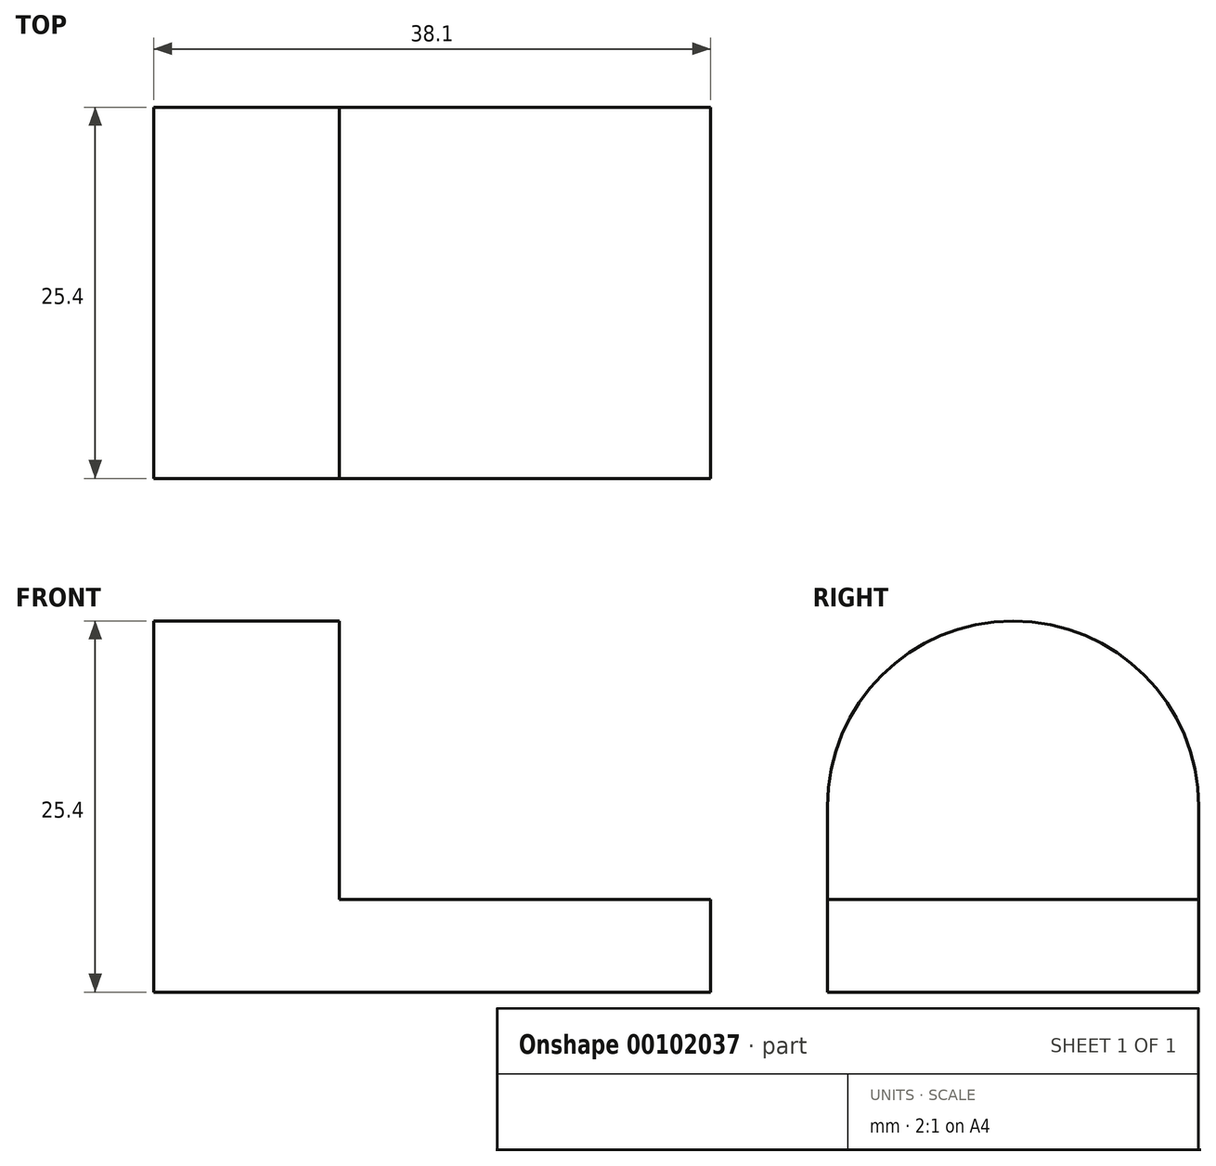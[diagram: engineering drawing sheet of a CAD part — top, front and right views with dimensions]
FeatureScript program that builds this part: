
annotation { "Feature Type Name" : "Feature", "Feature Type Description" : "" }
export const myFeature = defineFeature(function(context is Context, id is Id, definition is map)
    precondition{}
    {
        {
            var Q0;
            Q0=qCreatedBy(makeId("Right.planeOp"),FACE);
            var sketch = newSketch(context, id + "F0", { "sketchPlane" : qUnion([Q0])});
            skLineSegment(sketch, "E0", {"start": v(0, 0) * mm, "end": v(0, 12.7) * mm});
            skLineSegment(sketch, "E1", {"start": v(0, 0) * mm, "end": v(25.4, 0) * mm});
            skLineSegment(sketch, "E2", {"start": v(25.4, 0) * mm, "end": v(25.4, 12.7) * mm});
            skArc(sketch, "E3", {"start": v(25.4, 12.7) * mm, "mid": v(12.7, 25.4) * mm, "end": v(0, 12.7) * mm});
            skSolve(sketch);
        }
        {
            var Q0;
            Q0 = qSketchRegion(id + "F0", true);
            extrude(context, id + "F1", {"entities" : qUnion([Q0]), "depth" : 12.7 * mm});
        }
        {
            var Q0;
            Q0=makeQuery(id+"F1.opExtrude","CAP_FACE",FACE,{"disambiguationData":[OSD([sQuery(id+"F0.wireOp",EDGE,"E0"),sQuery(id+"F0.wireOp",EDGE,"E1"),sQuery(id+"F0.wireOp",EDGE,"E2"),sQuery(id+"F0.wireOp",EDGE,"E3")])],"isStart":false});
            var sketch = newSketch(context, id + "F2", { "sketchPlane" : qUnion([Q0])});
            skLineSegment(sketch, "E4.bottom", {"start": v(0, 0) * mm, "end": v(25.4, 0) * mm});
            skLineSegment(sketch, "E4.top", {"start": v(0, 6.35) * mm, "end": v(25.4, 6.35) * mm});
            skLineSegment(sketch, "E4.left", {"start": v(0, 0) * mm, "end": v(0, 6.35) * mm});
            skLineSegment(sketch, "E4.right", {"start": v(25.4, 0) * mm, "end": v(25.4, 6.35) * mm});
            skSolve(sketch);
        }
        {
            var Q0;
            Q0 = qSketchRegion(id + "F2", true);
            extrude(context, id + "F3", {"entities" : qUnion([Q0]), "operationType" : NewBodyOperationType.ADD, "depth" : 25.4 * mm});
        }
    });
